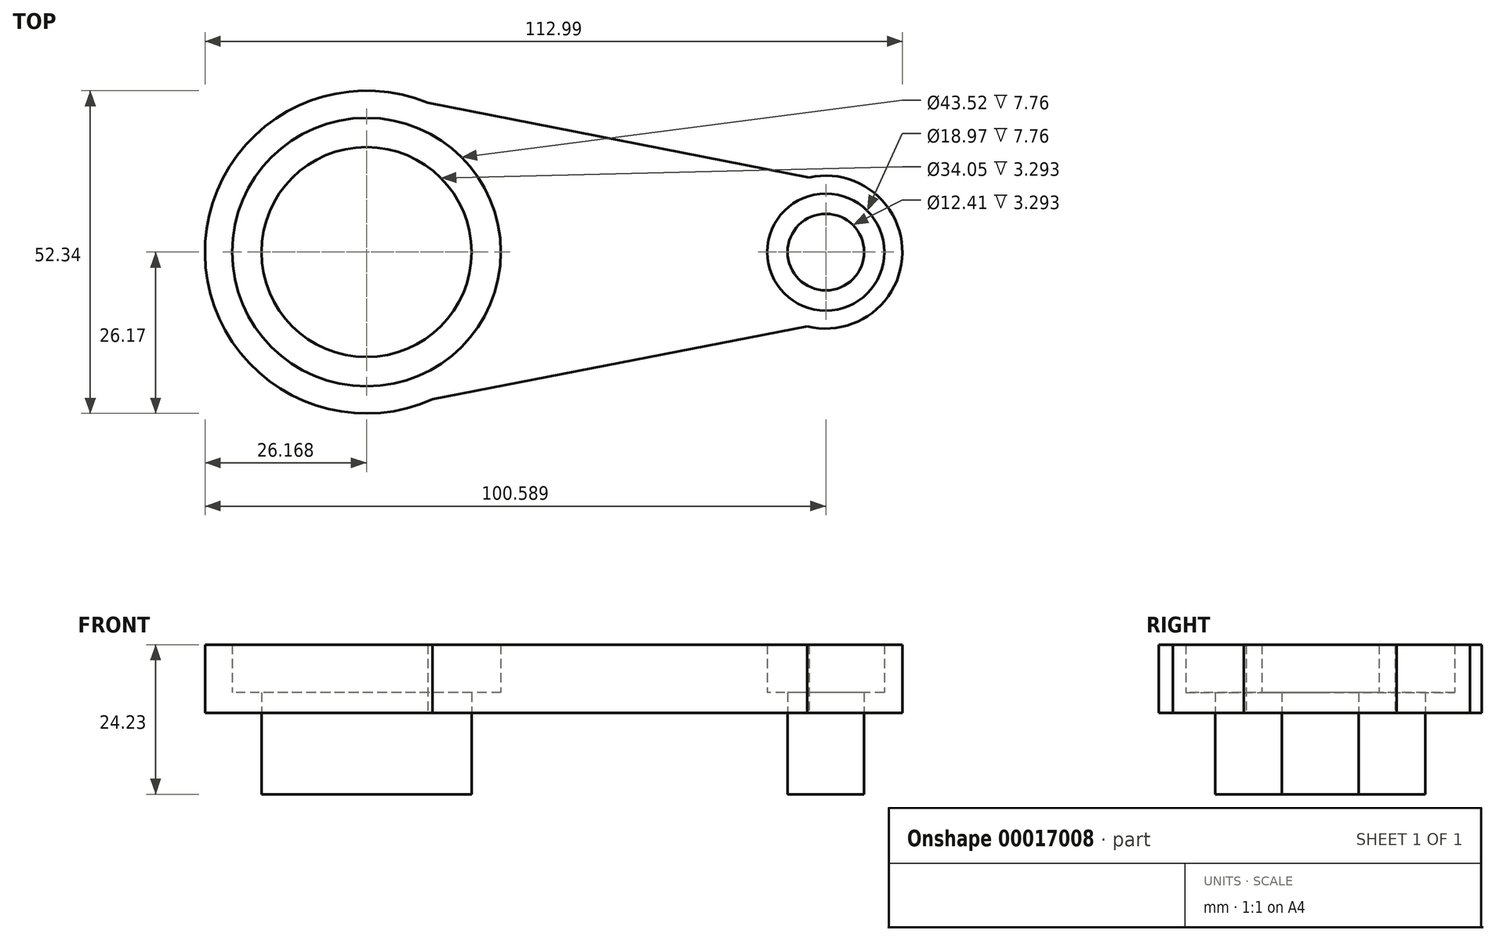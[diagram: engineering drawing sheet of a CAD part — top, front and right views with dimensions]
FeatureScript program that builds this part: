
annotation { "Feature Type Name" : "Feature", "Feature Type Description" : "" }
export const myFeature = defineFeature(function(context is Context, id is Id, definition is map)
    precondition{}
    {
        {
            var Q0;
            Q0=qCreatedBy(makeId("Top.planeOp"),FACE);
            var sketch = newSketch(context, id + "F0", { "sketchPlane" : qUnion([Q0])});
            skCircle(sketch, "E0", {"center": v(-43.68, 0) * mm, "radius": 26.17 * mm});
            skCircle(sketch, "E1", {"center": v(30.74, 0) * mm, "radius": 12.4 * mm});
            skLineSegment(sketch, "E2", {"start": v(-33.76, 24.21) * mm, "end": v(28.02, 12.1) * mm});
            skLineSegment(sketch, "E3", {"start": v(-32.98, -23.88) * mm, "end": v(27.71, -12.02) * mm});
            skCircle(sketch, "E4", {"center": v(-43.68, 0) * mm, "radius": 21.76 * mm});
            skCircle(sketch, "E5", {"center": v(-43.68, 0) * mm, "radius": 17.02 * mm});
            skCircle(sketch, "E6", {"center": v(30.74, 0) * mm, "radius": 9.49 * mm});
            skCircle(sketch, "E7", {"center": v(30.74, 0) * mm, "radius": 6.2 * mm});
            skSolve(sketch);
        }
        {
            var Q0;
            Q0 = qSketchRegion(id + "F0", true);
            extrude(context, id + "F1", {"entities" : qUnion([Q0]), "depth" : 11.05 * mm});
        }
        {
            var Q0;
            Q0=makeQuery(id+"F0.imprint","IMPRINT",FACE,{"disambiguationData":[TD([[makeQuery(id+"F0.imprint","IMPRINT",EDGE,{"derivedFrom":sQuery(id+"F0.wireOp",EDGE,"E6")}),1.0]])]});
            var Q1;
            Q1=makeQuery(id+"F0.imprint","IMPRINT",FACE,{"disambiguationData":[TD([[makeQuery(id+"F0.imprint","IMPRINT",EDGE,{"derivedFrom":sQuery(id+"F0.wireOp",EDGE,"E4")}),1.0]])]});
            extrude(context, id + "F2", {"entities" : qUnion([Q0, Q1]), "operationType" : NewBodyOperationType.ADD, "depth" : 3.3 * mm});
        }
        {
            var Q0;
            Q0=makeQuery(id+"F0.imprint","IMPRINT",FACE,{"disambiguationData":[TD([[makeQuery(id+"F0.imprint","IMPRINT",EDGE,{"derivedFrom":sQuery(id+"F0.wireOp",EDGE,"E7")}),1.0]])]});
            var Q1;
            Q1=makeQuery(id+"F0.imprint","IMPRINT",FACE,{"disambiguationData":[TD([[makeQuery(id+"F0.imprint","IMPRINT",EDGE,{"derivedFrom":sQuery(id+"F0.wireOp",EDGE,"E5")}),1.0]])]});
            extrude(context, id + "F3", {"entities" : qUnion([Q0, Q1]), "operationType" : NewBodyOperationType.ADD, "oppositeDirection" : true, "depth" : 13.18 * mm});
        }
    });
